# Revit family: ElectricalFixture_Hager_IP66SocketOutlets
name_source: partatom
category: Lighting Fixtures
revit_build: Autodesk Revit 2015 (Build: 20160512_1515(x64)
units: mm (PartAtom-declared; Revit-internal decimal feet)

## types (4) — shared parameters
1Gang = Yes
2 Gang = No
AssetType = Fixed
Back Plate Depth = 39 mm
Back Plate Height = 90 mm
Back Plate Width = 90 mm
Category = ElectricalFixture
ClassificationName = Uniclass2015
ClassificationValue = Pr_65_72_97
Colour = RAL9010WhiteGloss
Default Elevation = 500 mm
DocumentationCertificates = http://www.hager.co.uk
DocumentationLiterature = http://www.hager.co.uk
DocumentationTechnical = http://www.hager.co.uk
DurationUnit = Years
ExpectedLife = 25
Extrusion From Wall = 17 mm
Frequency = 50/60Hz
IfcExportAs = ElectricalFixture
IfcExportType = ElectricalFixture
Keynote = 16400
LED Indicator Switch = No
Manufacturer = Hager
ManufacturerName = Hager
Material = Urea Formaldehyde Thermoset Plastic
NBSDescription = ElectricalFixture
NBSReference = Pr_65_72_97
NominalDepth = 55 mm
NominalHeight = 115 mm
NominalWidth = 64 mm
One Way = No
Shape = Rectangular
Supply Phase = 1
Switch = Yes
Two Way = No
URL = http://www.hager.co.uk
Voltage = 230V/240V
WarrantyDescription = See Manufacturer
WarrantyDurationParts = 10
WarrantyDurationUnit = Years
WarrantyGuarantorParts = 10
_BimstoreBibleVersion = V14
_DistributedBy = www.bimstore.co.uk
zero-valued in all types: ReplacementCost, ServiceLifeDuration, Switch Height, Switch Width, WarrantyDurationLabor, _BimSpecGuid, _CurrentRevision

## per-type parameters (varying)
| type | BIMObjectName | Description | EAN | Features | NBSObjectName | NominalLength | TypeName |
| WXPS81 | Hager_ElectricalFixture_WXPS81 | IP66Single13AUnswitchedSocket | 3250617260060 | IP66Single13AUnswitchedSocket | Hager_IP66SocketOutlets_WXPS81 | 103 mm | ElectricalFixture_IP66SocketOutlets_WXPS81 |
| WXPS82 | Hager_ElectricalFixture_WXPS82 | IP66Twin13AUnswitchedSocket | 3250617260077 | IP66Twin13AUnswitchedSocket | Hager_IP66SocketOutlets_WXPS82 | 164 mm | ElectricalFixture_IP66SocketOutlets_WXPS82 |
| WXPSS81 | Hager_ElectricalFixture_WXPSS81 | IP66Single13ADoublePoleSwitchedSocket | 3250617260091 | IP66Single13ADoublePoleSwitchedSocket | Hager_IP66SocketOutlets_WXPSS81 | 103 mm | ElectricalFixture_IP66SocketOutlets_WXPSS81 |
| WXPSS82 | Hager_ElectricalFixture_WXPSS82 | IP66Twin13ADoublePoleSwitchedSocket | 3250617260107 | IP66Twin13ADoublePoleSwitchedSocket | Hager_IP66SocketOutlets_WXPSS82 | 164 mm | ElectricalFixture_IP66SocketOutlets_WXPS82 |

note: column(s) folded — value = type name in every type: Model, ModelNumber, ModelReference, Type Comments

## geometry (parser evidence)
native form markers: Blend x4, Extrusion x1, Sweep x2
no freeform markers — native parametric forms only
